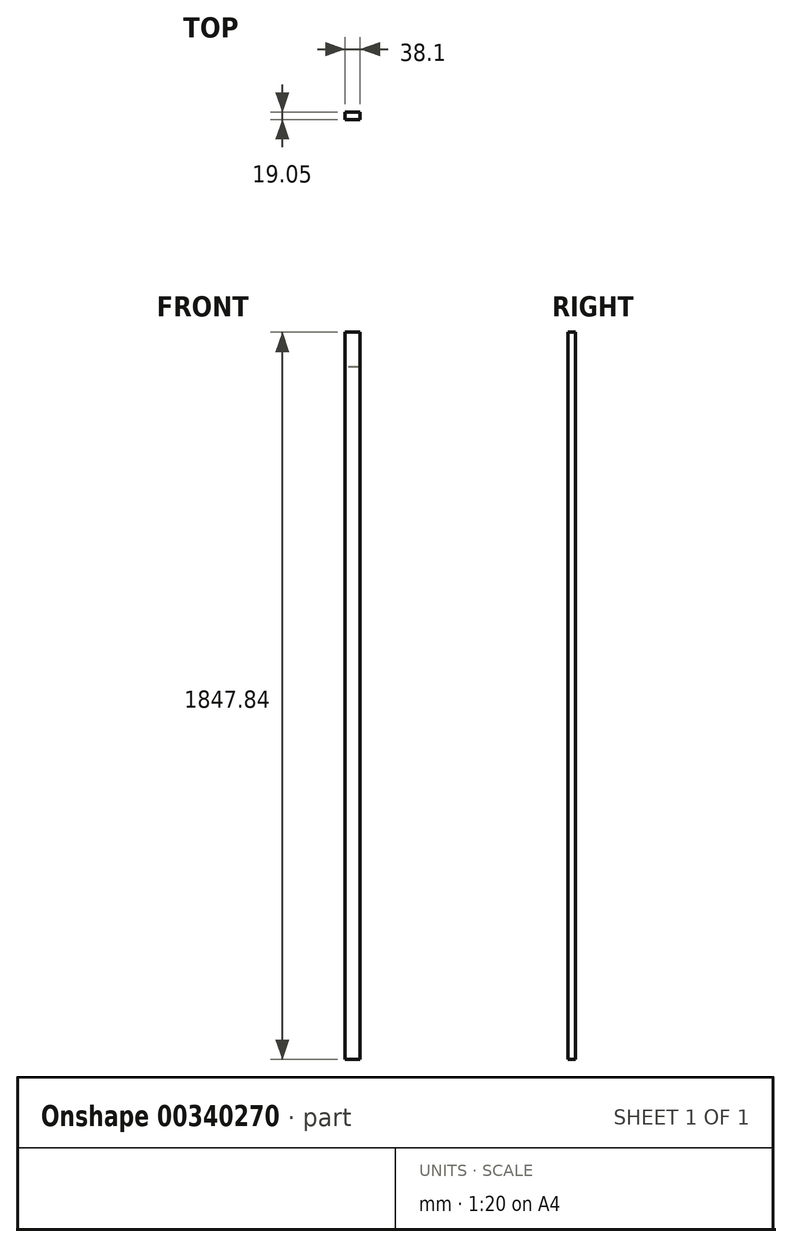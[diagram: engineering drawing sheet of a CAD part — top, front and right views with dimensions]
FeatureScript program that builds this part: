
annotation { "Feature Type Name" : "Feature", "Feature Type Description" : "" }
export const myFeature = defineFeature(function(context is Context, id is Id, definition is map)
    precondition{}
    {
        {
            var Q0;
            Q0=qCreatedBy(makeId("Front.planeOp"),FACE);
            var sketch = newSketch(context, id + "F0", { "sketchPlane" : qUnion([Q0])});
            skLineSegment(sketch, "E0.bottom", {"start": v(19.05, 923.93) * mm, "end": v(-19.05, 923.93) * mm});
            skLineSegment(sketch, "E0.top", {"start": v(19.05, -923.93) * mm, "end": v(-19.05, -923.93) * mm});
            skLineSegment(sketch, "E0.left", {"start": v(19.05, 923.93) * mm, "end": v(19.05, -923.93) * mm});
            skLineSegment(sketch, "E0.right", {"start": v(-19.05, 923.93) * mm, "end": v(-19.05, -923.93) * mm});
            skPoint(sketch, "E0.middle", {"position": v(0, 0) * mm});
            skSolve(sketch);
        }
        {
            var Q0;
            Q0 = qSketchRegion(id + "F0", true);
            extrude(context, id + "F1", {"entities" : qUnion([Q0]), "depth" : 19.05 * mm});
        }
        {
            var Q0;
            Q0=makeQuery(id+"F1.opExtrude","CAP_FACE",FACE,{"disambiguationData":[OSD([sQuery(id+"F0.wireOp",EDGE,"E0.bottom"),sQuery(id+"F0.wireOp",EDGE,"E0.top"),sQuery(id+"F0.wireOp",EDGE,"E0.left"),sQuery(id+"F0.wireOp",EDGE,"E0.right")])],"isStart":true});
            var sketch = newSketch(context, id + "F2", { "sketchPlane" : qUnion([Q0])});
            skLineSegment(sketch, "E1.bottom", {"start": v(-19.05, 923.93) * mm, "end": v(19.05, 923.93) * mm});
            skLineSegment(sketch, "E1.top", {"start": v(-19.05, 835.03) * mm, "end": v(19.05, 835.03) * mm});
            skLineSegment(sketch, "E1.left", {"start": v(-19.05, 923.93) * mm, "end": v(-19.05, 835.03) * mm});
            skLineSegment(sketch, "E1.right", {"start": v(19.05, 923.93) * mm, "end": v(19.05, 835.03) * mm});
            skSolve(sketch);
        }
        {
            var Q0;
            Q0 = qSketchRegion(id + "F2", true);
            extrude(context, id + "F3", {"entities" : qUnion([Q0]), "operationType" : NewBodyOperationType.REMOVE, "oppositeDirection" : true, "depth" : ((3 / 4) / 2) * mm});
        }
    });
